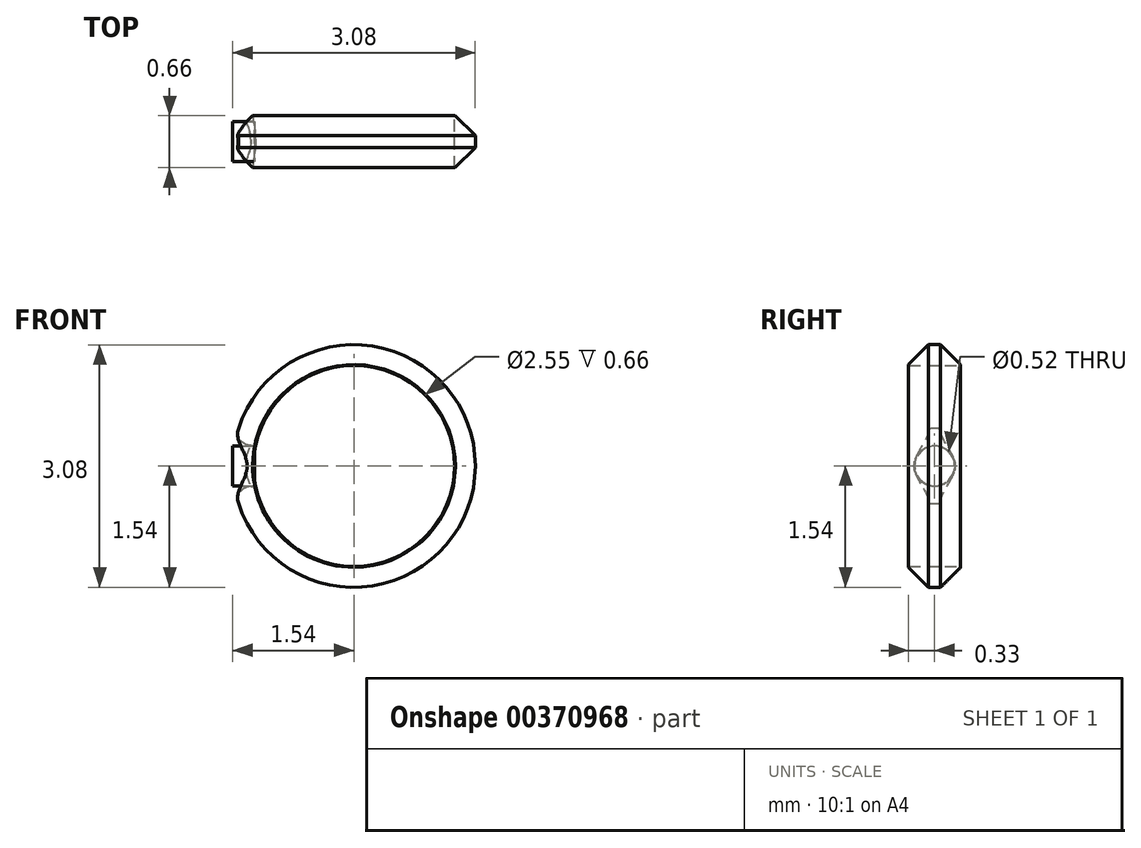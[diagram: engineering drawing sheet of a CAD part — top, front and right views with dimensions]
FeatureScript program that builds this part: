
annotation { "Feature Type Name" : "Feature", "Feature Type Description" : "" }
export const myFeature = defineFeature(function(context is Context, id is Id, definition is map)
    precondition{}
    {
        {
            var Q0;
            Q0=qCreatedBy(makeId("Front.planeOp"),FACE);
            var sketch = newSketch(context, id + "F0", { "sketchPlane" : qUnion([Q0])});
            skCircle(sketch, "E0", {"center": v(0, 0) * mm, "radius": 1.28 * mm});
            skCircle(sketch, "E1", {"center": v(0, 0) * mm, "radius": 1.54 * mm});
            skSolve(sketch);
        }
        {
            var Q0;
            Q0 = qSketchRegion(id + "F0", true);
            extrude(context, id + "F1", {"entities" : qUnion([Q0]), "endBound" : BoundingType.SYMMETRIC, "depth" : 0.66 * mm});
        }
        {
            var Q0;
            Q0=qCreatedBy(makeId("Right.planeOp"),FACE);
            var sketch = newSketch(context, id + "F2", { "sketchPlane" : qUnion([Q0])});
            skCircle(sketch, "E2", {"center": v(0, 0) * mm, "radius": 0.26 * mm});
            skSolve(sketch);
        }
        {
            var Q0;
            Q0 = qSketchRegion(id + "F2", true);
            extrude(context, id + "F3", {"entities" : qUnion([Q0]), "operationType" : NewBodyOperationType.REMOVE, "oppositeDirection" : true, "depth" : 1.94 * mm, "hasSecondDirection" : true, "secondDirectionOppositeDirection" : false, "secondDirectionDepth" : 1.13 * mm});
        }
        {
            var Q0;
            Q0=makeQuery(id+"F1.opExtrude","CAP_EDGE",EDGE,{"disambiguationData":[OSD([sQuery(id+"F0.wireOp",EDGE,"E1")])],"isStart":true});
            var Q1;
            Q1=makeQuery(id+"F1.opExtrude","CAP_EDGE",EDGE,{"disambiguationData":[OSD([sQuery(id+"F0.wireOp",EDGE,"E1")])],"isStart":false});
            chamfer(context, id + "F4", {"entities" : qUnion([Q0, Q1]), "width" : 0.25 * mm, "tangentPropagation" : true});
        }
        {
            var Q0;
            Q0=makeQuery(id+"F3.boolean.opBoolean","INTERSECT",EDGE,{"disambiguationData":[OD(0.0)],"derivedFrom":[makeQuery(id+"F1.opExtrude","SWEPT_FACE",FACE,{"disambiguationData":[OSD([sQuery(id+"F0.wireOp",EDGE,"E1")])]}),makeQuery(id+"F3.opExtrude","SWEPT_FACE",FACE,{"disambiguationData":[OSD([sQuery(id+"F2.wireOp",EDGE,"E2")])]})]});
            fillet(context, id + "F5", {"entities" : qUnion([Q0]), "radius" : 0.17 * mm, "tangentPropagation" : true, "allowEdgeOverflow" : false});
        }
        {
            var Q0;
            Q0=qCreatedBy(makeId("Right.planeOp"),FACE);
            var sketch = newSketch(context, id + "F6", { "sketchPlane" : qUnion([Q0])});
            skCircle(sketch, "E3", {"center": v(0, 0) * mm, "radius": 0.25 * mm});
            skSolve(sketch);
        }
        {
            var Q0;
            Q0 = qSketchRegion(id + "F6", true);
            extrude(context, id + "F7", {"entities" : qUnion([Q0]), "oppositeDirection" : true, "depth" : 1.54 * mm, "hasSecondDirection" : true, "secondDirectionOppositeDirection" : true, "secondDirectionDepth" : 1.26 * mm});
        }
    });
